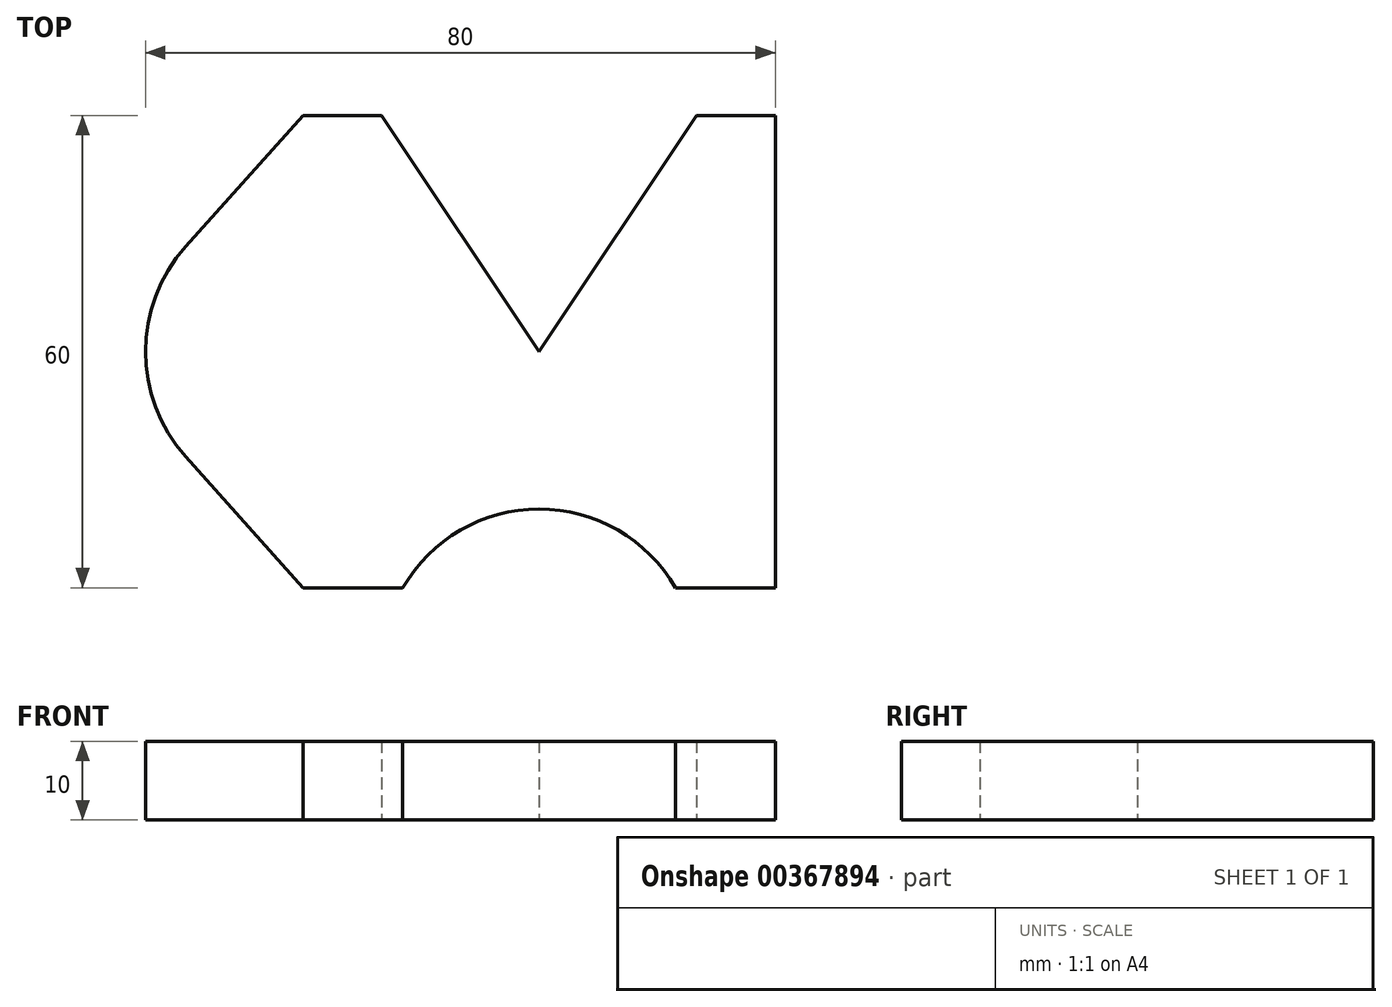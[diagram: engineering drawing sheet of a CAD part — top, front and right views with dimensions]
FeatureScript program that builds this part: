
annotation { "Feature Type Name" : "Feature", "Feature Type Description" : "" }
export const myFeature = defineFeature(function(context is Context, id is Id, definition is map)
    precondition{}
    {
        {
            var Q0;
            Q0=qCreatedBy(makeId("Top.planeOp"),FACE);
            var sketch = newSketch(context, id + "F0", { "sketchPlane" : qUnion([Q0])});
            skLineSegment(sketch, "E0", {"start": v(-30, 30) * mm, "end": v(-20, 30) * mm});
            skLineSegment(sketch, "E1", {"start": v(-20, 30) * mm, "end": v(0, 0) * mm});
            skLineSegment(sketch, "E2", {"start": v(0, 0) * mm, "end": v(20, 30) * mm});
            skLineSegment(sketch, "E3", {"start": v(20, 30) * mm, "end": v(30, 30) * mm});
            skLineSegment(sketch, "E4", {"start": v(30, 30) * mm, "end": v(30, -30) * mm});
            skLineSegment(sketch, "E5", {"start": v(30, -30) * mm, "end": v(17.32, -30) * mm});
            skLineSegment(sketch, "E6", {"start": v(-17.32, -30) * mm, "end": v(-30, -30) * mm});
            skLineSegment(sketch, "E7", {"start": v(-30, -30) * mm, "end": v(-44.9, -13.33) * mm});
            skArc(sketch, "E8", {"start": v(17.32, -30) * mm, "mid": v(0, -20) * mm, "end": v(-17.32, -30) * mm});
            skArc(sketch, "E9", {"start": v(-44.9, 13.33) * mm, "mid": v(-50, 0) * mm, "end": v(-44.9, -13.33) * mm});
            skLineSegment(sketch, "E10", {"start": v(-30, 30) * mm, "end": v(-44.9, 13.33) * mm});
            skLineSegment(sketch, "E11", {"start": v(-30, 30) * mm, "end": v(-30, -30) * mm, "construction": true});
            skSolve(sketch);
        }
        {
            var Q0;
            Q0=makeQuery(id+"F0.imprint","IMPRINT",FACE,{"disambiguationData":[TD([[makeQuery(id+"F0.imprint","IMPRINT",EDGE,{"derivedFrom":sQuery(id+"F0.wireOp",EDGE,"E0")}),-1.0]])]});
            extrude(context, id + "F1", {"entities" : qUnion([Q0]), "depth" : 10 * mm});
        }
    });
